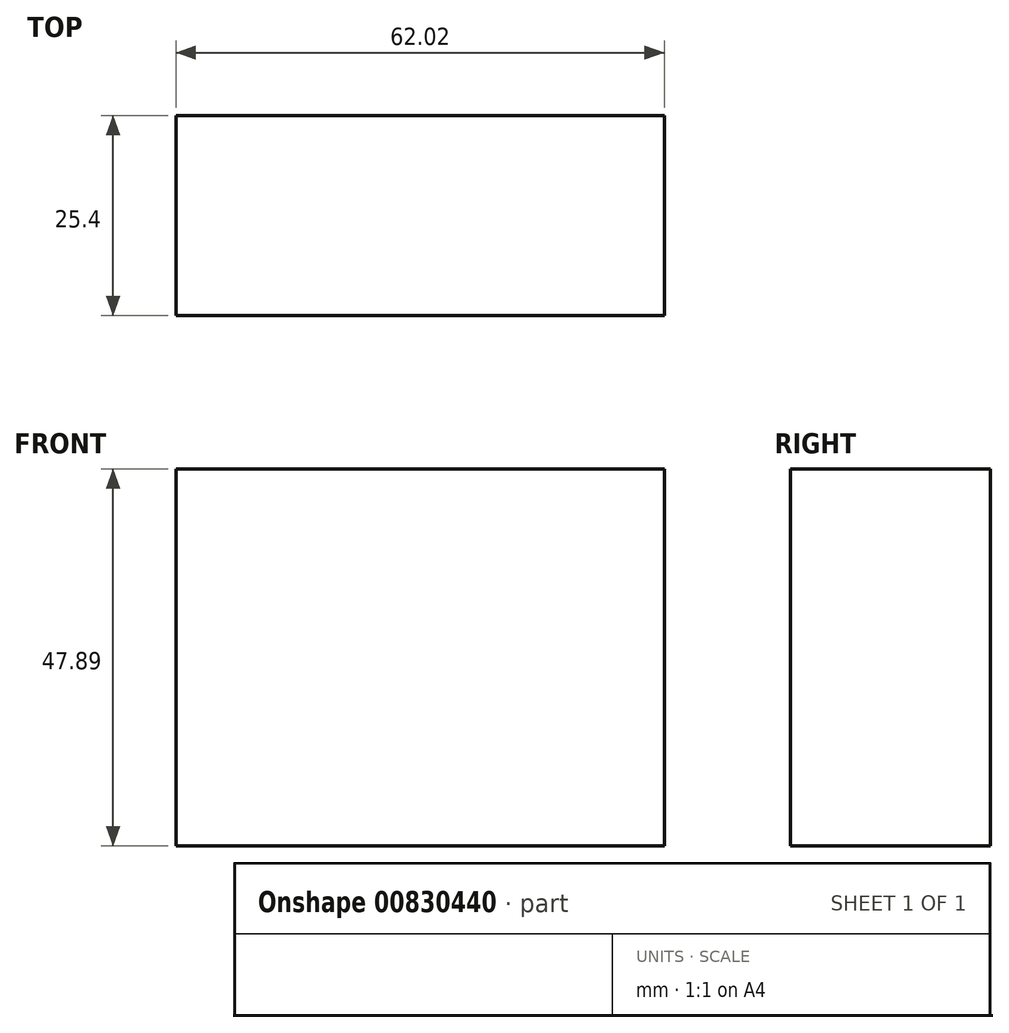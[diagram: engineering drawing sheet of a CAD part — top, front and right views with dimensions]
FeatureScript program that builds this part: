
annotation { "Feature Type Name" : "Feature", "Feature Type Description" : "" }
export const myFeature = defineFeature(function(context is Context, id is Id, definition is map)
    precondition{}
    {
        {
            var Q0;
            Q0=qCreatedBy(makeId("Front.planeOp"),FACE);
            var sketch = newSketch(context, id + "F0", { "sketchPlane" : qUnion([Q0])});
            skLineSegment(sketch, "E0.bottom", {"start": v(0, 47.89) * mm, "end": v(62.02, 47.89) * mm});
            skLineSegment(sketch, "E0.top", {"start": v(0, 0) * mm, "end": v(62.02, 0) * mm});
            skLineSegment(sketch, "E0.left", {"start": v(0, 47.89) * mm, "end": v(0, 0) * mm});
            skLineSegment(sketch, "E0.right", {"start": v(62.02, 47.89) * mm, "end": v(62.02, 0) * mm});
            skSolve(sketch);
        }
        {
            var Q0;
            Q0 = qSketchRegion(id + "F0", true);
            extrude(context, id + "F1", {"entities" : qUnion([Q0]), "depth" : 25.4 * mm, "offsetDistance" : 25.4 * mm});
        }
    });
